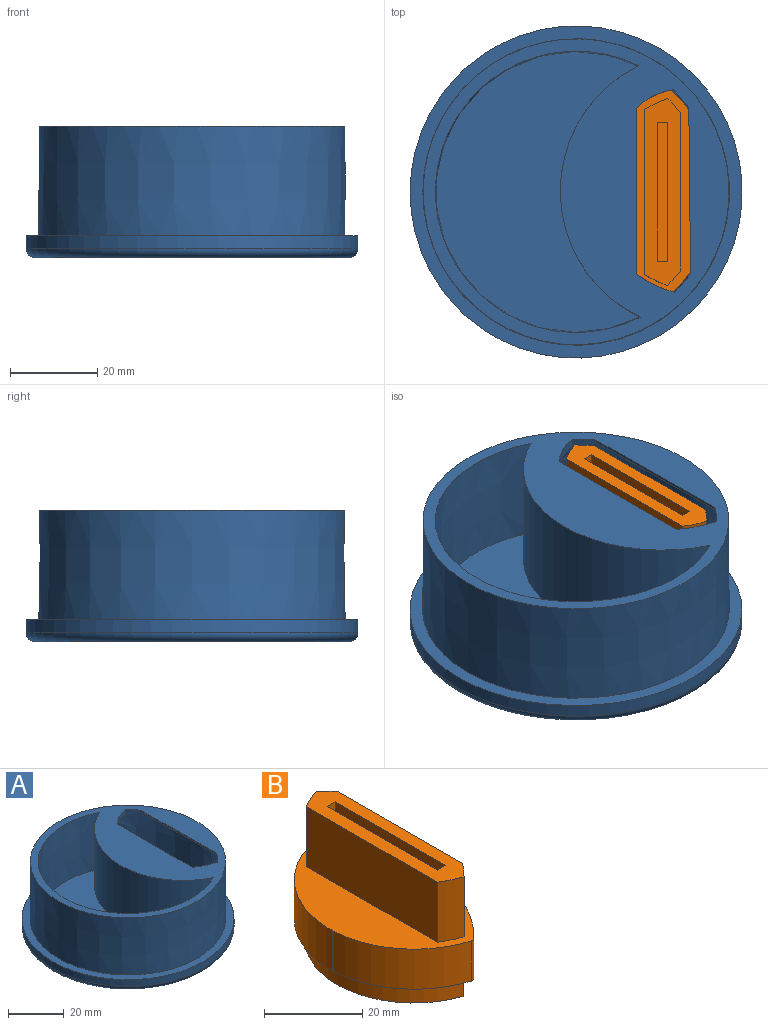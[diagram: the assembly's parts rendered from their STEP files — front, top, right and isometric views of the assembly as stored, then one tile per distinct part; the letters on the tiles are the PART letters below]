
ASSEMBLY  parts=2 mates=1
PART A: 46 faces, bbox 82.5x82.5x30.3 mm
  f0: cone r=32.1mm half-angle=0.2deg, axis (0,0,1), area 1273.2mm2, adj f1,f2,f3,f4,f31,f32,f33,f37
  f1: cylinder r=26.88mm len=50.95mm, axis (0,0,1), area 1338.1mm2, adj f0,f4,f33,f44
  f2: plane 38.07x0.6mm, normal (-1,-0.01,0), area 22.8mm2, adj f0,f37,f38
  f3: plane 12.03x0.63mm, normal (0,0,-1), area 4.6mm2, adj f0,f43
  f4: plane 50.89x30.75mm, normal (0,0,1), area 150.6mm2, adj f0,f1,f12,f13,f14,f15,f16,f17
  f5: plane 72x72mm, normal (0,0,-1), area 3320.6mm2, adj f11,f24,f25,f26,f27,f28,f29
  f6: plane 64.24x46.69mm, normal (0,0,1), area 1771.3mm2, adj f9,f30
  f7: cylinder r=38mm len=76mm, axis (0,0,-1), area 716.3mm2, adj f8,f11
  f8: plane 76x76mm, normal (0,0,1), area 669.8mm2, adj f7,f10
  f9: cone r=32.1mm half-angle=0.2deg, axis (0,0,1), area 3275mm2, adj f6,f30,f37
  f10: cone r=35.1mm half-angle=0.2deg, axis (0,0,-1), area 5503.9mm2, adj f8,f37
  f11: torus R=36mm, axis (0,0,-1), area 735.7mm2, adj f5,f7
  f12: plane 1.92x0.1mm, normal (1,0,0), area 0.2mm2, adj f4,f13,f22,f23
  f13: cylinder r=24.5mm len=0.24mm, axis (0,0,1), area 0mm2, adj f4,f12,f14,f23
  f14: plane 0.1x0mm, normal (1,0.04,0), area 0mm2, adj f4,f13,f15,f23
  f15: cylinder r=24.5mm len=22.38mm, axis (0,0,1), area 3mm2, adj f4,f14,f16,f23
  f16: cylinder r=1mm len=0.97mm, axis (0,0,1), area 0.1mm2, adj f4,f15,f17,f23
  f17: cylinder r=31.92mm len=22.1mm, axis (0,0,1), area 2.5mm2, adj f4,f16,f18,f23
  f18: plane 2.26x0.1mm, normal (-1,0,0), area 0.2mm2, adj f4,f17,f19,f23
  f19: cylinder r=31.92mm len=22.13mm, axis (0,0,1), area 2.5mm2, adj f4,f18,f20,f23
  f20: cylinder r=1mm len=0.97mm, axis (0,0,1), area 0.1mm2, adj f4,f19,f21,f23
  f21: cylinder r=24.5mm len=22.33mm, axis (0,0,1), area 3mm2, adj f4,f20,f22,f23
  f22: plane 0.1x0.08mm, normal (1,-0.05,0), area 0mm2, adj f4,f12,f21,f23
  f23: plane 47.03x28.47mm, normal (0,0,1), area 221.1mm2, adj f12,f13,f14,f15,f16,f17,f18,f19
  f24: cylinder r=29.92mm len=18.24mm, axis (0,0,1), area 101.4mm2, adj f5,f23,f25,f29
  f25: plane 4.9x2mm, normal (-1,0.08,0), area 9.8mm2, adj f5,f23,f24,f26
  f26: plane 4.9x2.26mm, normal (-1,0,0), area 11mm2, adj f5,f23,f25,f27
  f27: plane 4.9x2mm, normal (-1,-0.08,0), area 9.8mm2, adj f5,f23,f26,f28
  f28: cylinder r=29.92mm len=18.27mm, axis (0,0,1), area 101.4mm2, adj f5,f23,f27,f29
  f29: cylinder r=22.5mm len=42.77mm, axis (0,0,1), area 276.7mm2, adj f5,f23,f24,f28
  f30: cylinder r=31.88mm len=57.52mm, axis (0,0,1), area 1789.9mm2, adj f6,f9,f37
  f31: plane 3.09x0.42mm, normal (0.36,0.93,0), area 0.8mm2, adj f0,f34,f37,f42
  f32: cylinder r=15.44mm len=9.83mm, axis (0,0,1), area 20.6mm2, adj f0,f36,f37,f39,f44
  f33: plane 46.79x18.47mm, normal (0,0,-1), area 139.2mm2, adj f0,f1,f40,f44,f45
  f34: plane 2.33x0.25mm, normal (0.26,0.96,0), area 0.6mm2, adj f31,f35,f37,f42
  f35: cylinder r=23.87mm len=9.62mm, axis (0,0,1), area 19.9mm2, adj f34,f36,f37,f39,f40,f41
  f36: plane 37.93x0.6mm, normal (1,0,0), area 22.8mm2, adj f32,f35,f37,f39
  f37: plane 69.99x69.99mm, normal (0,0,1), area 1540mm2, adj f0,f2,f9,f10,f30,f31,f32,f34
  f38: plane 38.06x3.86mm, normal (-0.71,-0.01,-0.71), area 161.5mm2, adj f0,f2,f43
  f39: plane 38.13x3.14mm, normal (0.71,0,-0.71), area 145.9mm2, adj f32,f35,f36,f40,f44,f45
  f40: torus R=26.87mm, axis (0,0,1), area 59.2mm2, adj f33,f35,f39,f41,f45
  f41: bspline ~3x2.85mm, area 3.2mm2, adj f0,f35,f40,f42
  f42: bspline ~4.11x2.99mm, area 2.8mm2, adj f0,f31,f34,f41
  f43: cylinder r=3mm len=25.79mm, axis (-0.01,1,0), area 44.5mm2, adj f0,f3,f38
  f44: torus R=18.44mm, axis (0,0,1), area 64.9mm2, adj f0,f1,f32,f33,f39,f45
  f45: cylinder r=5mm len=32.79mm, axis (0,1,0), area 125.6mm2, adj f33,f39,f40,f44
PART B: 32 faces, bbox 28.5x47x30 mm
  f0: plane 5x1.99mm, normal (1,-0.08,0), area 10mm2, adj f1,f4,f6,f7
  f1: plane 5x2.24mm, normal (1,0,0), area 11.2mm2, adj f0,f2,f6,f7
  f2: plane 5x1.99mm, normal (1,0.08,0), area 10mm2, adj f1,f3,f6,f7
  f3: cylinder r=29.72mm len=18.06mm, axis (0,0,1), area 102.1mm2, adj f2,f5,f6,f7
  f4: cylinder r=29.72mm len=18.03mm, axis (0,0,1), area 102.2mm2, adj f0,f5,f6,f7
  f5: cylinder r=22.3mm len=42.31mm, axis (0,0,1), area 278.6mm2, adj f3,f4,f6,f7
  f6: plane 42.31x24.1mm, normal (0,0,-1), area 730.2mm2, adj f0,f1,f2,f3,f4,f5
  f7: plane 47.03x28.47mm, normal (0,0,-1), area 241.8mm2, adj f0,f1,f2,f3,f4,f5,f8,f9
  f8: plane 10x1.92mm, normal (-1,0,0), area 19.2mm2, adj f7,f9,f18,f31
  f9: cylinder r=24.5mm len=10mm, axis (0,0,-1), area 2.4mm2, adj f7,f8,f10,f31
  f10: plane 10x0mm, normal (-1,-0.04,0), area 0mm2, adj f7,f9,f11,f31
  f11: cylinder r=24.5mm len=22.38mm, axis (0,0,-1), area 302.4mm2, adj f7,f10,f12,f31
  f12: cylinder r=1mm len=10mm, axis (0,0,-1), area 10.5mm2, adj f7,f11,f13,f31
  f13: cylinder r=31.92mm len=22.1mm, axis (0,0,-1), area 249.2mm2, adj f7,f12,f14,f31
  f14: plane 10x2.26mm, normal (1,0,0), area 22.6mm2, adj f7,f13,f15,f31
  f15: cylinder r=31.92mm len=22.13mm, axis (0,0,-1), area 249mm2, adj f7,f14,f16,f31
  f16: cylinder r=1mm len=10mm, axis (0,0,-1), area 10.5mm2, adj f7,f15,f17,f31
  f17: cylinder r=24.5mm len=22.33mm, axis (0,0,-1), area 302.6mm2, adj f7,f16,f18,f31
  f18: plane 10x0.08mm, normal (-1,0.05,0), area 0.8mm2, adj f7,f8,f17,f31
  f19: plane 31.75x2.3mm, normal (0,0,1), area 73mm2, adj f21,f22,f23,f24
  f20: plane 42.77x8.3mm, normal (0,0,1), area 260.2mm2, adj f21,f22,f23,f24,f25,f26,f27,f28
  f21: plane 20x2.3mm, normal (0,-1,0), area 46mm2, adj f19,f20,f22,f24
  f22: plane 31.75x20mm, normal (1,0,0), area 635mm2, adj f19,f20,f21,f23
  f23: plane 20x2.3mm, normal (0,1,0), area 46mm2, adj f19,f20,f22,f24
  f24: plane 31.75x20mm, normal (-1,0,0), area 635mm2, adj f19,f20,f21,f23
  f25: plane 35.79x15mm, normal (1,0,0), area 536.9mm2, adj f20,f28,f29,f31
  f26: plane 37.76x15mm, normal (-1,0,0), area 566.3mm2, adj f20,f27,f30,f31
  f27: cylinder r=22.5mm len=15mm, axis (0,0,-1), area 88.1mm2, adj f20,f26,f28,f31
  f28: cylinder r=29.92mm len=15mm, axis (0,0,-1), area 68.7mm2, adj f20,f25,f27,f31
  f29: cylinder r=29.92mm len=15mm, axis (0,0,-1), area 70.5mm2, adj f20,f25,f30,f31
  f30: cylinder r=22.5mm len=15mm, axis (0,0,-1), area 86.8mm2, adj f20,f26,f29,f31
  f31: plane 47.03x28.47mm, normal (0,0,1), area 638.8mm2, adj f8,f9,f10,f11,f12,f13,f14,f15
PLACE A at identity fixed
PLACE B at identity
MATE slider B.f20 <-> A.f37  axis (0,0,1) through (15.67,-18.93,30)mm
